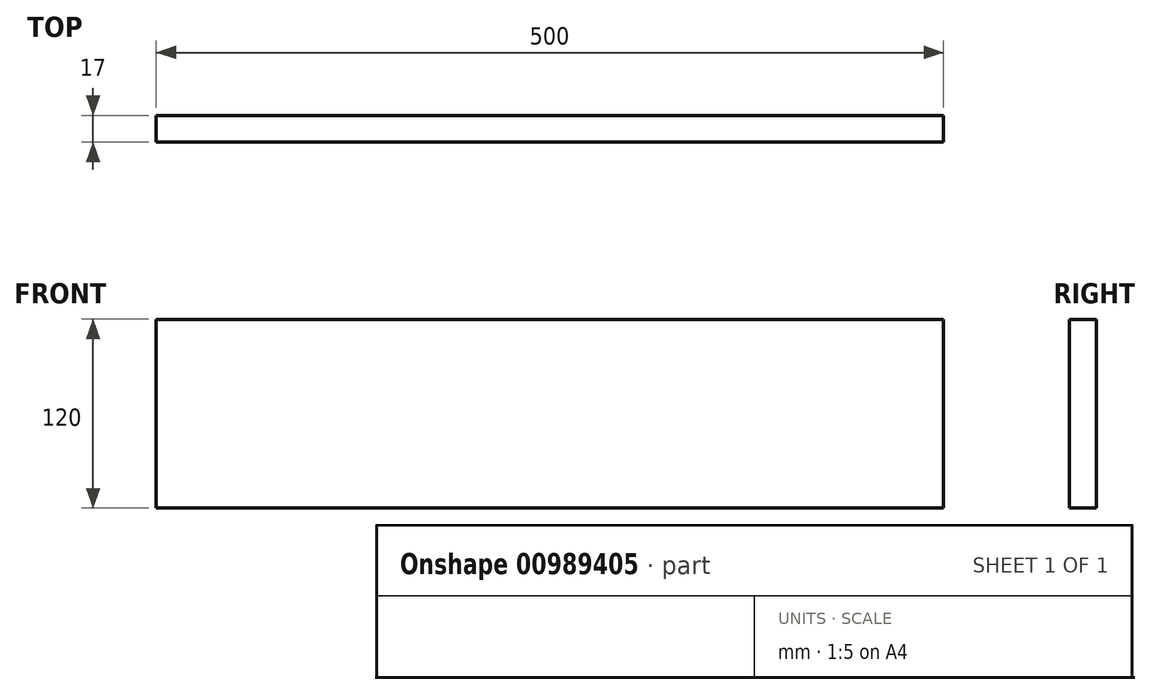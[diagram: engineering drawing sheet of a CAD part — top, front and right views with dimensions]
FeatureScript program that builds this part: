
annotation { "Feature Type Name" : "Feature", "Feature Type Description" : "" }
export const myFeature = defineFeature(function(context is Context, id is Id, definition is map)
    precondition{}
    {
        {
            var Q0;
            Q0=qCreatedBy(makeId("Front.planeOp"),FACE);
            var sketch = newSketch(context, id + "F0", { "sketchPlane" : qUnion([Q0])});
            skLineSegment(sketch, "E0.bottom", {"start": v(-58.26, -30.41) * mm, "end": v(-558.26, -30.41) * mm});
            skLineSegment(sketch, "E0.top", {"start": v(-58.26, 89.59) * mm, "end": v(-558.26, 89.59) * mm});
            skLineSegment(sketch, "E0.left", {"start": v(-58.26, -30.41) * mm, "end": v(-58.26, 89.59) * mm});
            skLineSegment(sketch, "E0.right", {"start": v(-558.26, -30.41) * mm, "end": v(-558.26, 89.59) * mm});
            skPoint(sketch, "E0.middle", {"position": v(-308.26, 29.59) * mm});
            skSolve(sketch);
        }
        {
            var Q0;
            Q0 = qSketchRegion(id + "F0", true);
            var Q1;
            Q1=makeQuery(id+"F0.imprint","IMPRINT",FACE,{"disambiguationData":[TD([[makeQuery(id+"F0.imprint","IMPRINT",EDGE,{"derivedFrom":sQuery(id+"F0.wireOp",EDGE,"E0.bottom")}),-1.0]])]});
            extrude(context, id + "F1", {"entities" : qUnion([Q0, Q1]), "depth" : 17 * mm, "offsetDistance" : 25 * mm});
        }
    });
